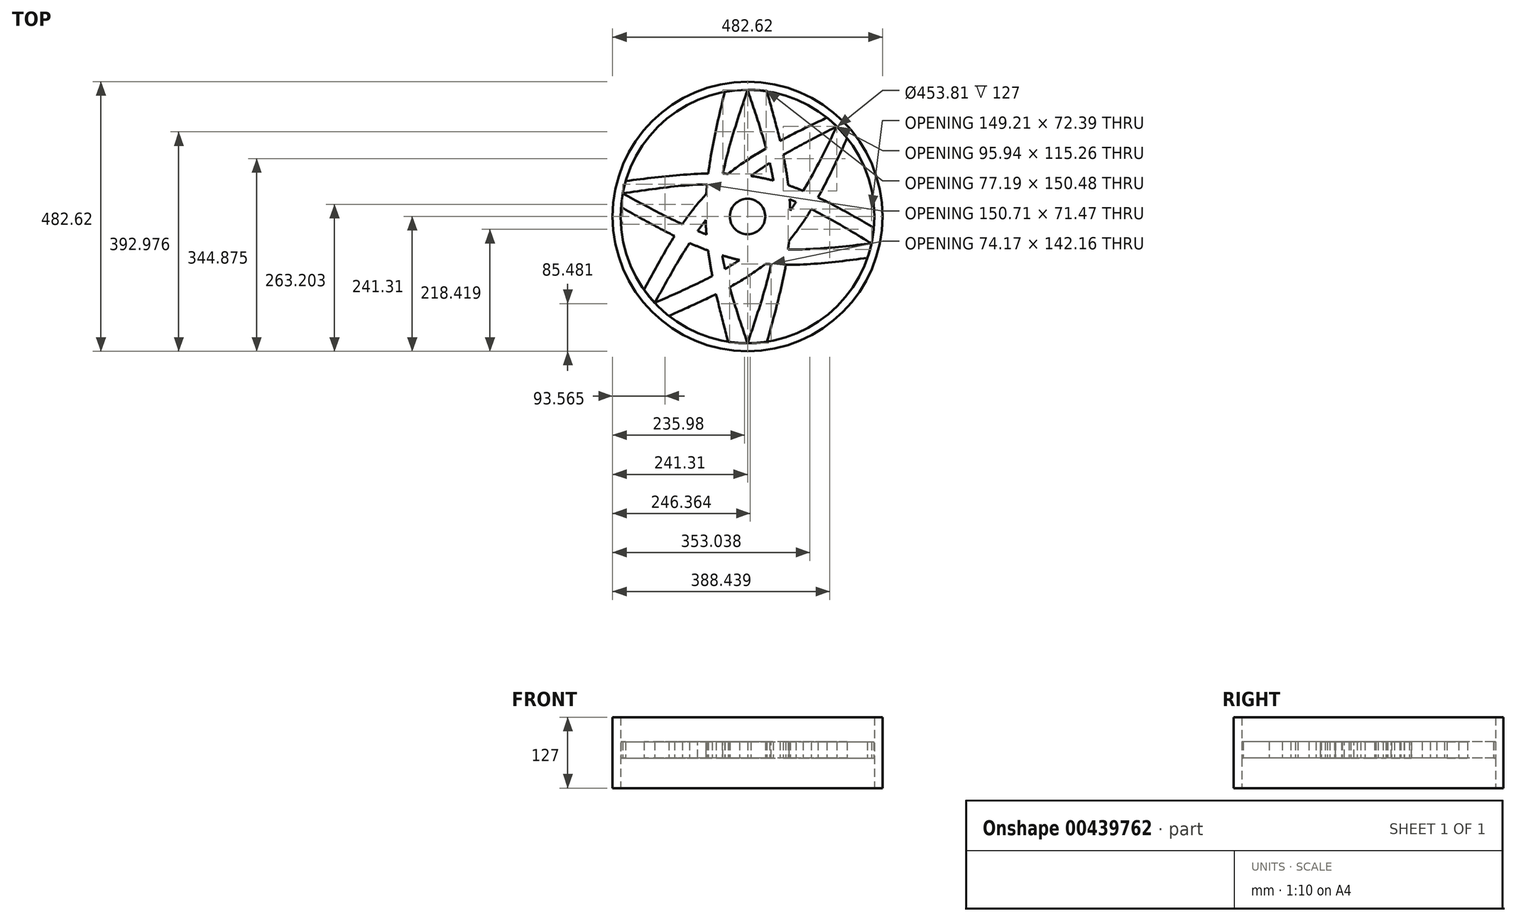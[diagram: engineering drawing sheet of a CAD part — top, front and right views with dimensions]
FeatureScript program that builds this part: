
annotation { "Feature Type Name" : "Feature", "Feature Type Description" : "" }
export const myFeature = defineFeature(function(context is Context, id is Id, definition is map)
    precondition{}
    {
        {
            var Q0;
            Q0=qCreatedBy(makeId("Top.planeOp"),FACE);
            var sketch = newSketch(context, id + "F0", { "sketchPlane" : qUnion([Q0])});
            skCircle(sketch, "E0", {"center": v(0, 0) * mm, "radius": 241.31 * mm});
            skCircle(sketch, "E1", {"center": v(0, 0) * mm, "radius": 31.77 * mm});
            skCircle(sketch, "E2", {"center": v(0, 0) * mm, "radius": 226.9 * mm});
            skFitSpline(sketch, "E3", {"points": [v(0, 226.9) * mm, v(-51.98, 0) * mm, v(0, -226.9) * mm], "startDerivative": vector(-152.5, -453.81) * mm, "endDerivative": vector(152.5, -453.81) * mm});
            skFitSpline(sketch, "E4", {"points": [v(0, 226.9) * mm, v(51.98, 0) * mm, v(0, -226.9) * mm], "startDerivative": vector(152.5, -453.81) * mm, "endDerivative": vector(-152.5, -453.81) * mm});
            skFitSpline(sketch, "E5", {"points": [v(-41.03, 223.17) * mm, v(-75, 0) * mm, v(-34.75, -224.23) * mm], "startDerivative": vector(-105.1, -447.44) * mm, "endDerivative": vector(117.58, -447.2) * mm});
            skFitSpline(sketch, "E6", {"points": [v(34.55, 224.26) * mm, v(76.47, 0) * mm, v(34.75, -224.23) * mm], "startDerivative": vector(125.73, -448.2) * mm, "endDerivative": vector(-125.27, -448.46) * mm});
            skFitSpline(sketch, "E7", {"points": [v(159.7, 161.2) * mm, v(-35.94, 37.55) * mm, v(-166, -154.7) * mm], "startDerivative": vector(-422.02, -215.9) * mm, "endDerivative": vector(-229.15, -415.66) * mm});
            skFitSpline(sketch, "E8", {"points": [v(142, 177) * mm, v(-58.52, 55.73) * mm, v(-185.22, -131.08) * mm], "startDerivative": vector(-432.84, -205.47) * mm, "endDerivative": vector(-220.65, -410.99) * mm});
            skFitSpline(sketch, "E9", {"points": [v(159.7, 161.2) * mm, v(32.57, -40.5) * mm, v(-166, -154.7) * mm], "startDerivative": vector(-208.67, -433.82) * mm, "endDerivative": vector(-442.51, -198.17) * mm});
            skFitSpline(sketch, "E10", {"points": [v(178.3, 140.33) * mm, v(54.6, -64.67) * mm, v(-140.7, -178.02) * mm], "startDerivative": vector(-205.55, -439.17) * mm, "endDerivative": vector(-432.46, -196.4) * mm});
            skFitSpline(sketch, "E11", {"points": [v(-223.1, 41.39) * mm, v(-6.94, -51.51) * mm, v(221.73, -48.18) * mm], "startDerivative": vector(421.7, -229.62) * mm, "endDerivative": vector(467.5, 51.27) * mm});
            skFitSpline(sketch, "E12", {"points": [v(-223.1, 41.39) * mm, v(10.2, 50.96) * mm, v(221.73, -48.18) * mm], "startDerivative": vector(476.9, 70.05) * mm, "endDerivative": vector(412.78, -249.16) * mm});
            skFitSpline(sketch, "E13", {"points": [v(-226.28, 16.81) * mm, v(-7.33, -79.24) * mm, v(214.47, -74.08) * mm], "startDerivative": vector(424, -239.26) * mm, "endDerivative": vector(457.26, 59.44) * mm});
            skFitSpline(sketch, "E14", {"points": [v(-217.83, 63.55) * mm, v(23.66, 69.54) * mm, v(226.02, -20.1) * mm], "startDerivative": vector(487.4, 61.66) * mm, "endDerivative": vector(399.3, -230.98) * mm});
            skSolve(sketch);
        }
        {
            var Q0;
            Q0=makeQuery(id+"F0.imprint","IMPRINT",FACE,{"disambiguationData":[TD([[makeQuery(id+"F0.imprint","IMPRINT",EDGE,{"derivedFrom":sQuery(id+"F0.wireOp",EDGE,"E0")}),1.0]])]});
            extrude(context, id + "F1", {"entities" : qUnion([Q0]), "depth" : 63.5 * mm, "hasSecondDirection" : true, "secondDirectionOppositeDirection" : true, "secondDirectionDepth" : 63.5 * mm});
        }
        {
            var Q0;
            {var subQ0=sQuery(id+"F0.wireOp",EDGE,"E11");var subQ5=sQuery(id+"F0.wireOp",EDGE,"E8");var subQ7=makeQuery(id+"F0.imprint","INTERSECT",VERTEX,{"derivedFrom":[subQ5,subQ0]});Q0=makeQuery(id+"F0.imprint","IMPRINT",FACE,{"disambiguationData":[TD([[makeQuery(id+"F0.imprint","IMPRINT",EDGE,{"disambiguationData":[TD([[subQ7,-1.0]])],"derivedFrom":subQ5}),-1.0]])]});}
            var Q1;
            {var subQ1=sQuery(id+"F0.wireOp",EDGE,"E2");var subQ3=sQuery(id+"F0.wireOp",EDGE,"E8");var subQ4=makeQuery(id+"F0.imprint","INTERSECT",VERTEX,{"disambiguationData":[OD(1.0)],"derivedFrom":[subQ1,subQ3]});Q1=makeQuery(id+"F0.imprint","IMPRINT",FACE,{"disambiguationData":[TD([[makeQuery(id+"F0.imprint","IMPRINT",EDGE,{"disambiguationData":[TD([[subQ4,1.0]])],"derivedFrom":subQ3}),1.0]])]});}
            var Q2;
            {var subQ0=sQuery(id+"F0.wireOp",EDGE,"E11");var subQ1=sQuery(id+"F0.wireOp",EDGE,"E7");var subQ2=makeQuery(id+"F0.imprint","INTERSECT",VERTEX,{"derivedFrom":[subQ1,subQ0]});Q2=makeQuery(id+"F0.imprint","IMPRINT",FACE,{"disambiguationData":[TD([[makeQuery(id+"F0.imprint","IMPRINT",EDGE,{"disambiguationData":[TD([[subQ2,-1.0]])],"derivedFrom":subQ1}),-1.0]])]});}
            var Q3;
            {var subQ0=sQuery(id+"F0.wireOp",EDGE,"E9");var subQ5=sQuery(id+"F0.wireOp",EDGE,"E5");var subQ6=makeQuery(id+"F0.imprint","INTERSECT",VERTEX,{"derivedFrom":[subQ5,subQ0]});Q3=makeQuery(id+"F0.imprint","IMPRINT",FACE,{"disambiguationData":[TD([[makeQuery(id+"F0.imprint","IMPRINT",EDGE,{"disambiguationData":[TD([[subQ6,-1.0]])],"derivedFrom":subQ5}),-1.0]])]});}
            var Q4;
            {var subQ0=sQuery(id+"F0.wireOp",EDGE,"E9");var subQ1=sQuery(id+"F0.wireOp",EDGE,"E3");var subQ2=makeQuery(id+"F0.imprint","INTERSECT",VERTEX,{"derivedFrom":[subQ1,subQ0]});Q4=makeQuery(id+"F0.imprint","IMPRINT",FACE,{"disambiguationData":[TD([[makeQuery(id+"F0.imprint","IMPRINT",EDGE,{"disambiguationData":[TD([[subQ2,-1.0]])],"derivedFrom":subQ1}),-1.0]])]});}
            var Q5;
            {var subQ1=sQuery(id+"F0.wireOp",EDGE,"E2");var subQ3=sQuery(id+"F0.wireOp",EDGE,"E5");var subQ4=makeQuery(id+"F0.imprint","INTERSECT",VERTEX,{"disambiguationData":[OD(1.0)],"derivedFrom":[subQ1,subQ3]});Q5=makeQuery(id+"F0.imprint","IMPRINT",FACE,{"disambiguationData":[TD([[makeQuery(id+"F0.imprint","IMPRINT",EDGE,{"disambiguationData":[TD([[subQ4,1.0]])],"derivedFrom":subQ3}),1.0]])]});}
            var Q6;
            {var subQ0=sQuery(id+"F0.wireOp",EDGE,"E11");var subQ1=sQuery(id+"F0.wireOp",EDGE,"E4");var subQ2=makeQuery(id+"F0.imprint","INTERSECT",VERTEX,{"derivedFrom":[subQ1,subQ0]});Q6=makeQuery(id+"F0.imprint","IMPRINT",FACE,{"disambiguationData":[TD([[makeQuery(id+"F0.imprint","IMPRINT",EDGE,{"disambiguationData":[TD([[subQ2,-1.0]])],"derivedFrom":subQ1}),1.0]])]});}
            var Q7;
            {var subQ3=sQuery(id+"F0.wireOp",EDGE,"E14");var subQ5=sQuery(id+"F0.wireOp",EDGE,"E10");var subQ7=makeQuery(id+"F0.imprint","INTERSECT",VERTEX,{"derivedFrom":[subQ5,subQ3]});Q7=makeQuery(id+"F0.imprint","IMPRINT",FACE,{"disambiguationData":[TD([[makeQuery(id+"F0.imprint","IMPRINT",EDGE,{"disambiguationData":[TD([[subQ7,-1.0]])],"derivedFrom":subQ5}),1.0]])]});}
            var Q8;
            {var subQ1=sQuery(id+"F0.wireOp",EDGE,"E2");var subQ3=sQuery(id+"F0.wireOp",EDGE,"E10");var subQ4=makeQuery(id+"F0.imprint","INTERSECT",VERTEX,{"disambiguationData":[OD(0.0)],"derivedFrom":[subQ1,subQ3]});Q8=makeQuery(id+"F0.imprint","IMPRINT",FACE,{"disambiguationData":[TD([[makeQuery(id+"F0.imprint","IMPRINT",EDGE,{"disambiguationData":[TD([[subQ4,-1.0]])],"derivedFrom":subQ3}),-1.0]])]});}
            var Q9;
            {var subQ0=sQuery(id+"F0.wireOp",EDGE,"E14");var subQ1=sQuery(id+"F0.wireOp",EDGE,"E9");var subQ2=makeQuery(id+"F0.imprint","INTERSECT",VERTEX,{"derivedFrom":[subQ1,subQ0]});Q9=makeQuery(id+"F0.imprint","IMPRINT",FACE,{"disambiguationData":[TD([[makeQuery(id+"F0.imprint","IMPRINT",EDGE,{"disambiguationData":[TD([[subQ2,-1.0]])],"derivedFrom":subQ1}),1.0]])]});}
            var Q10;
            {var subQ3=sQuery(id+"F0.wireOp",EDGE,"E10");var subQ7=sQuery(id+"F0.wireOp",EDGE,"E4");var subQ8=makeQuery(id+"F0.imprint","INTERSECT",VERTEX,{"derivedFrom":[subQ7,subQ3]});Q10=makeQuery(id+"F0.imprint","IMPRINT",FACE,{"disambiguationData":[TD([[makeQuery(id+"F0.imprint","IMPRINT",EDGE,{"disambiguationData":[TD([[subQ8,-1.0]])],"derivedFrom":subQ7}),1.0]])]});}
            var Q11;
            {var subQ1=sQuery(id+"F0.wireOp",EDGE,"E2");var subQ3=sQuery(id+"F0.wireOp",EDGE,"E6");var subQ4=makeQuery(id+"F0.imprint","INTERSECT",VERTEX,{"disambiguationData":[OD(1.0)],"derivedFrom":[subQ1,subQ3]});Q11=makeQuery(id+"F0.imprint","IMPRINT",FACE,{"disambiguationData":[TD([[makeQuery(id+"F0.imprint","IMPRINT",EDGE,{"disambiguationData":[TD([[subQ4,1.0]])],"derivedFrom":subQ3}),-1.0]])]});}
            var Q12;
            {var subQ0=sQuery(id+"F0.wireOp",EDGE,"E11");var subQ5=sQuery(id+"F0.wireOp",EDGE,"E6");var subQ7=makeQuery(id+"F0.imprint","INTERSECT",VERTEX,{"derivedFrom":[subQ5,subQ0]});Q12=makeQuery(id+"F0.imprint","IMPRINT",FACE,{"disambiguationData":[TD([[makeQuery(id+"F0.imprint","IMPRINT",EDGE,{"disambiguationData":[TD([[subQ7,-1.0]])],"derivedFrom":subQ5}),1.0]])]});}
            var Q13;
            {var subQ3=sQuery(id+"F0.wireOp",EDGE,"E8");var subQ5=sQuery(id+"F0.wireOp",EDGE,"E6");var subQ7=makeQuery(id+"F0.imprint","INTERSECT",VERTEX,{"derivedFrom":[subQ5,subQ3]});Q13=makeQuery(id+"F0.imprint","IMPRINT",FACE,{"disambiguationData":[TD([[makeQuery(id+"F0.imprint","IMPRINT",EDGE,{"disambiguationData":[TD([[subQ7,-1.0]])],"derivedFrom":subQ5}),1.0]])]});}
            var Q14;
            {var subQ0=sQuery(id+"F0.wireOp",EDGE,"E8");var subQ1=sQuery(id+"F0.wireOp",EDGE,"E4");var subQ2=makeQuery(id+"F0.imprint","INTERSECT",VERTEX,{"derivedFrom":[subQ1,subQ0]});Q14=makeQuery(id+"F0.imprint","IMPRINT",FACE,{"disambiguationData":[TD([[makeQuery(id+"F0.imprint","IMPRINT",EDGE,{"disambiguationData":[TD([[subQ2,-1.0]])],"derivedFrom":subQ1}),1.0]])]});}
            var Q15;
            {var subQ1=sQuery(id+"F0.wireOp",EDGE,"E2");var subQ3=sQuery(id+"F0.wireOp",EDGE,"E6");var subQ4=makeQuery(id+"F0.imprint","INTERSECT",VERTEX,{"disambiguationData":[OD(0.0)],"derivedFrom":[subQ1,subQ3]});Q15=makeQuery(id+"F0.imprint","IMPRINT",FACE,{"disambiguationData":[TD([[makeQuery(id+"F0.imprint","IMPRINT",EDGE,{"disambiguationData":[TD([[subQ4,-1.0]])],"derivedFrom":subQ3}),-1.0]])]});}
            var Q16;
            {var subQ1=sQuery(id+"F0.wireOp",EDGE,"E2");var subQ3=sQuery(id+"F0.wireOp",EDGE,"E5");var subQ4=makeQuery(id+"F0.imprint","INTERSECT",VERTEX,{"disambiguationData":[OD(0.0)],"derivedFrom":[subQ1,subQ3]});Q16=makeQuery(id+"F0.imprint","IMPRINT",FACE,{"disambiguationData":[TD([[makeQuery(id+"F0.imprint","IMPRINT",EDGE,{"disambiguationData":[TD([[subQ4,-1.0]])],"derivedFrom":subQ3}),1.0]])]});}
            var Q17;
            {var subQ5=sQuery(id+"F0.wireOp",EDGE,"E3");var subQ7=sQuery(id+"F0.wireOp",EDGE,"E14");var subQ9=makeQuery(id+"F0.imprint","INTERSECT",VERTEX,{"derivedFrom":[subQ5,subQ7]});Q17=makeQuery(id+"F0.imprint","IMPRINT",FACE,{"disambiguationData":[TD([[makeQuery(id+"F0.imprint","IMPRINT",EDGE,{"disambiguationData":[TD([[subQ9,-1.0]])],"derivedFrom":subQ5}),-1.0]])]});}
            var Q18;
            {var subQ3=sQuery(id+"F0.wireOp",EDGE,"E14");var subQ5=sQuery(id+"F0.wireOp",EDGE,"E5");var subQ6=makeQuery(id+"F0.imprint","INTERSECT",VERTEX,{"derivedFrom":[subQ5,subQ3]});Q18=makeQuery(id+"F0.imprint","IMPRINT",FACE,{"disambiguationData":[TD([[makeQuery(id+"F0.imprint","IMPRINT",EDGE,{"disambiguationData":[TD([[subQ6,-1.0]])],"derivedFrom":subQ5}),-1.0]])]});}
            var Q19;
            {var subQ0=sQuery(id+"F0.wireOp",EDGE,"E8");var subQ1=sQuery(id+"F0.wireOp",EDGE,"E3");var subQ2=makeQuery(id+"F0.imprint","INTERSECT",VERTEX,{"derivedFrom":[subQ1,subQ0]});Q19=makeQuery(id+"F0.imprint","IMPRINT",FACE,{"disambiguationData":[TD([[makeQuery(id+"F0.imprint","IMPRINT",EDGE,{"disambiguationData":[TD([[subQ2,-1.0]])],"derivedFrom":subQ1}),-1.0]])]});}
            var Q20;
            {var subQ0=sQuery(id+"F0.wireOp",EDGE,"E8");var subQ1=sQuery(id+"F0.wireOp",EDGE,"E5");var subQ2=makeQuery(id+"F0.imprint","INTERSECT",VERTEX,{"derivedFrom":[subQ1,subQ0]});Q20=makeQuery(id+"F0.imprint","IMPRINT",FACE,{"disambiguationData":[TD([[makeQuery(id+"F0.imprint","IMPRINT",EDGE,{"disambiguationData":[TD([[subQ2,-1.0]])],"derivedFrom":subQ1}),-1.0]])]});}
            var Q21;
            {var subQ0=sQuery(id+"F0.wireOp",EDGE,"E8");var subQ1=sQuery(id+"F0.wireOp",EDGE,"E4");var subQ2=makeQuery(id+"F0.imprint","INTERSECT",VERTEX,{"derivedFrom":[subQ1,subQ0]});Q21=makeQuery(id+"F0.imprint","IMPRINT",FACE,{"disambiguationData":[TD([[makeQuery(id+"F0.imprint","IMPRINT",EDGE,{"disambiguationData":[TD([[subQ2,-1.0]])],"derivedFrom":subQ1}),-1.0]])]});}
            var Q22;
            {var subQ0=sQuery(id+"F0.wireOp",EDGE,"E9");var subQ1=sQuery(id+"F0.wireOp",EDGE,"E3");var subQ2=makeQuery(id+"F0.imprint","INTERSECT",VERTEX,{"derivedFrom":[subQ1,subQ0]});Q22=makeQuery(id+"F0.imprint","IMPRINT",FACE,{"disambiguationData":[TD([[makeQuery(id+"F0.imprint","IMPRINT",EDGE,{"disambiguationData":[TD([[subQ2,-1.0]])],"derivedFrom":subQ1}),1.0]])]});}
            var Q23;
            {var subQ0=sQuery(id+"F0.wireOp",EDGE,"E9");var subQ1=sQuery(id+"F0.wireOp",EDGE,"E6");var subQ2=makeQuery(id+"F0.imprint","INTERSECT",VERTEX,{"derivedFrom":[subQ1,subQ0]});Q23=makeQuery(id+"F0.imprint","IMPRINT",FACE,{"disambiguationData":[TD([[makeQuery(id+"F0.imprint","IMPRINT",EDGE,{"disambiguationData":[TD([[subQ2,-1.0]])],"derivedFrom":subQ1}),1.0]])]});}
            var Q24;
            {var subQ0=sQuery(id+"F0.wireOp",EDGE,"E7");var subQ1=sQuery(id+"F0.wireOp",EDGE,"E4");var subQ2=makeQuery(id+"F0.imprint","INTERSECT",VERTEX,{"derivedFrom":[subQ1,subQ0]});Q24=makeQuery(id+"F0.imprint","IMPRINT",FACE,{"disambiguationData":[TD([[makeQuery(id+"F0.imprint","IMPRINT",EDGE,{"disambiguationData":[TD([[subQ2,-1.0]])],"derivedFrom":subQ1}),1.0]])]});}
            var Q25;
            {var subQ0=sQuery(id+"F0.wireOp",EDGE,"E13");var subQ1=sQuery(id+"F0.wireOp",EDGE,"E3");var subQ2=makeQuery(id+"F0.imprint","INTERSECT",VERTEX,{"derivedFrom":[subQ1,subQ0]});Q25=makeQuery(id+"F0.imprint","IMPRINT",FACE,{"disambiguationData":[TD([[makeQuery(id+"F0.imprint","IMPRINT",EDGE,{"disambiguationData":[TD([[subQ2,-1.0]])],"derivedFrom":subQ1}),-1.0]])]});}
            var Q26;
            {var subQ0=sQuery(id+"F0.wireOp",EDGE,"E11");var subQ1=sQuery(id+"F0.wireOp",EDGE,"E5");var subQ2=makeQuery(id+"F0.imprint","INTERSECT",VERTEX,{"derivedFrom":[subQ1,subQ0]});Q26=makeQuery(id+"F0.imprint","IMPRINT",FACE,{"disambiguationData":[TD([[makeQuery(id+"F0.imprint","IMPRINT",EDGE,{"disambiguationData":[TD([[subQ2,-1.0]])],"derivedFrom":subQ1}),-1.0]])]});}
            var Q27;
            {var subQ0=sQuery(id+"F0.wireOp",EDGE,"E14");var subQ1=sQuery(id+"F0.wireOp",EDGE,"E6");var subQ2=makeQuery(id+"F0.imprint","INTERSECT",VERTEX,{"derivedFrom":[subQ1,subQ0]});Q27=makeQuery(id+"F0.imprint","IMPRINT",FACE,{"disambiguationData":[TD([[makeQuery(id+"F0.imprint","IMPRINT",EDGE,{"disambiguationData":[TD([[subQ2,-1.0]])],"derivedFrom":subQ1}),1.0]])]});}
            var Q28;
            {var subQ0=sQuery(id+"F0.wireOp",EDGE,"E12");var subQ1=sQuery(id+"F0.wireOp",EDGE,"E5");var subQ2=makeQuery(id+"F0.imprint","INTERSECT",VERTEX,{"derivedFrom":[subQ1,subQ0]});Q28=makeQuery(id+"F0.imprint","IMPRINT",FACE,{"disambiguationData":[TD([[makeQuery(id+"F0.imprint","IMPRINT",EDGE,{"disambiguationData":[TD([[subQ2,-1.0]])],"derivedFrom":subQ1}),1.0]])]});}
            var Q29;
            {var subQ0=sQuery(id+"F0.wireOp",EDGE,"E14");var subQ1=sQuery(id+"F0.wireOp",EDGE,"E3");var subQ2=makeQuery(id+"F0.imprint","INTERSECT",VERTEX,{"derivedFrom":[subQ1,subQ0]});Q29=makeQuery(id+"F0.imprint","IMPRINT",FACE,{"disambiguationData":[TD([[makeQuery(id+"F0.imprint","IMPRINT",EDGE,{"disambiguationData":[TD([[subQ2,-1.0]])],"derivedFrom":subQ1}),1.0]])]});}
            var Q30;
            {var subQ0=sQuery(id+"F0.wireOp",EDGE,"E10");var subQ1=sQuery(id+"F0.wireOp",EDGE,"E4");var subQ2=makeQuery(id+"F0.imprint","INTERSECT",VERTEX,{"derivedFrom":[subQ1,subQ0]});Q30=makeQuery(id+"F0.imprint","IMPRINT",FACE,{"disambiguationData":[TD([[makeQuery(id+"F0.imprint","IMPRINT",EDGE,{"disambiguationData":[TD([[subQ2,-1.0]])],"derivedFrom":subQ1}),-1.0]])]});}
            var Q31;
            {var subQ0=sQuery(id+"F0.wireOp",EDGE,"E10");var subQ1=sQuery(id+"F0.wireOp",EDGE,"E6");var subQ2=makeQuery(id+"F0.imprint","INTERSECT",VERTEX,{"derivedFrom":[subQ1,subQ0]});Q31=makeQuery(id+"F0.imprint","IMPRINT",FACE,{"disambiguationData":[TD([[makeQuery(id+"F0.imprint","IMPRINT",EDGE,{"disambiguationData":[TD([[subQ2,-1.0]])],"derivedFrom":subQ1}),-1.0]])]});}
            var Q32;
            {var subQ0=sQuery(id+"F0.wireOp",EDGE,"E7");var subQ1=sQuery(id+"F0.wireOp",EDGE,"1zvcAR7V-laDh-ktkW-U6ED-mYYCZ9MNF7Ux");var subQ5=makeQuery(id+"F0.imprint","INTERSECT",VERTEX,{"disambiguationData":[OD(0.0)],"derivedFrom":[subQ1,subQ0]});Q32=makeQuery(id+"F0.imprint","IMPRINT",FACE,{"disambiguationData":[TD([[makeQuery(id+"F0.imprint","IMPRINT",EDGE,{"disambiguationData":[TD([[subQ5,-1.0]])],"derivedFrom":subQ1}),-1.0]])]});}
            var Q33;
            {var subQ1=sQuery(id+"F0.wireOp",EDGE,"E4");var subQ7=makeQuery(id+"F0.imprint","INTERSECT",VERTEX,{"derivedFrom":[sQuery(id+"F0.wireOp",EDGE,"1zvcAR7V-laDh-ktkW-U6ED-mYYCZ9MNF7Ux"),subQ1]});Q33=makeQuery(id+"F0.imprint","IMPRINT",FACE,{"disambiguationData":[TD([[makeQuery(id+"F0.imprint","IMPRINT",EDGE,{"disambiguationData":[TD([[subQ7,1.0]])],"derivedFrom":subQ1}),1.0]])]});}
            var Q34;
            {var subQ0=sQuery(id+"F0.wireOp",EDGE,"E11");var subQ1=sQuery(id+"F0.wireOp",EDGE,"1zvcAR7V-laDh-ktkW-U6ED-mYYCZ9MNF7Ux");var subQ2=makeQuery(id+"F0.imprint","INTERSECT",VERTEX,{"disambiguationData":[OD(0.0)],"derivedFrom":[subQ1,subQ0]});Q34=makeQuery(id+"F0.imprint","IMPRINT",FACE,{"disambiguationData":[TD([[makeQuery(id+"F0.imprint","IMPRINT",EDGE,{"disambiguationData":[TD([[subQ2,-1.0]])],"derivedFrom":subQ1}),-1.0]])]});}
            var Q35;
            {var subQ0=sQuery(id+"F0.wireOp",EDGE,"E11");var subQ1=sQuery(id+"F0.wireOp",EDGE,"E3");var subQ2=makeQuery(id+"F0.imprint","INTERSECT",VERTEX,{"derivedFrom":[subQ1,subQ0]});Q35=makeQuery(id+"F0.imprint","IMPRINT",FACE,{"disambiguationData":[TD([[makeQuery(id+"F0.imprint","IMPRINT",EDGE,{"disambiguationData":[TD([[subQ2,-1.0]])],"derivedFrom":subQ1}),1.0]])]});}
            var Q36;
            {var subQ0=sQuery(id+"F0.wireOp",EDGE,"E9");var subQ1=sQuery(id+"F0.wireOp",EDGE,"E4");var subQ2=makeQuery(id+"F0.imprint","INTERSECT",VERTEX,{"derivedFrom":[subQ1,subQ0]});Q36=makeQuery(id+"F0.imprint","IMPRINT",FACE,{"disambiguationData":[TD([[makeQuery(id+"F0.imprint","IMPRINT",EDGE,{"disambiguationData":[TD([[subQ2,-1.0]])],"derivedFrom":subQ1}),-1.0]])]});}
            var Q37;
            {var subQ0=sQuery(id+"F0.wireOp",EDGE,"E12");var subQ1=sQuery(id+"F0.wireOp",EDGE,"E4");var subQ2=makeQuery(id+"F0.imprint","INTERSECT",VERTEX,{"derivedFrom":[subQ1,subQ0]});Q37=makeQuery(id+"F0.imprint","IMPRINT",FACE,{"disambiguationData":[TD([[makeQuery(id+"F0.imprint","IMPRINT",EDGE,{"disambiguationData":[TD([[subQ2,-1.0]])],"derivedFrom":subQ1}),1.0]])]});}
            extrude(context, id + "F2", {"entities" : qUnion([Q0, Q1, Q2, Q3, Q4, Q5, Q6, Q7, Q8, Q9, Q10, Q11, Q12, Q13, Q14, Q15, Q16, Q17, Q18, Q19, Q20, Q21, Q22, Q23, Q24, Q25, Q26, Q27, Q28, Q29, Q30, Q31, Q32, Q33, Q34, Q35, Q36, Q37]), "depth" : 9.7 * mm, "hasSecondDirection" : true, "secondDirectionOppositeDirection" : true, "secondDirectionDepth" : 9.7 * mm});
        }
        {
            var Q0;
            {var subQ3=sQuery(id+"F0.wireOp",EDGE,"E12");var subQ5=sQuery(id+"F0.wireOp",EDGE,"E3");var subQ6=makeQuery(id+"F0.imprint","INTERSECT",VERTEX,{"derivedFrom":[subQ5,subQ3]});Q0=makeQuery(id+"F0.imprint","IMPRINT",FACE,{"disambiguationData":[TD([[makeQuery(id+"F0.imprint","IMPRINT",EDGE,{"disambiguationData":[TD([[subQ6,-1.0]])],"derivedFrom":subQ5}),-1.0]])]});}
            extrude(context, id + "F3", {"entities" : qUnion([Q0]), "depth" : 9.7 * mm, "hasSecondDirection" : true, "secondDirectionOppositeDirection" : true, "secondDirectionDepth" : 9.7 * mm});
        }
        {
            var Q0;
            {var subQ0=sQuery(id+"F0.wireOp",EDGE,"E14");var subQ1=sQuery(id+"F0.wireOp",EDGE,"E4");var subQ2=makeQuery(id+"F0.imprint","INTERSECT",VERTEX,{"derivedFrom":[subQ1,subQ0]});Q0=makeQuery(id+"F0.imprint","IMPRINT",FACE,{"disambiguationData":[TD([[makeQuery(id+"F0.imprint","IMPRINT",EDGE,{"disambiguationData":[TD([[subQ2,-1.0]])],"derivedFrom":subQ1}),1.0]])]});}
            var Q1;
            {var subQ0=sQuery(id+"F0.wireOp",EDGE,"E12");var subQ1=sQuery(id+"F0.wireOp",EDGE,"E4");var subQ2=makeQuery(id+"F0.imprint","INTERSECT",VERTEX,{"derivedFrom":[subQ1,subQ0]});Q1=makeQuery(id+"F0.imprint","IMPRINT",FACE,{"disambiguationData":[TD([[makeQuery(id+"F0.imprint","IMPRINT",EDGE,{"disambiguationData":[TD([[subQ2,-1.0]])],"derivedFrom":subQ1}),1.0]])]});}
            var Q2;
            {var subQ5=sQuery(id+"F0.wireOp",EDGE,"E9");var subQ6=sQuery(id+"F0.wireOp",EDGE,"E4");var subQ7=makeQuery(id+"F0.imprint","INTERSECT",VERTEX,{"derivedFrom":[subQ6,subQ5]});Q2=makeQuery(id+"F0.imprint","IMPRINT",FACE,{"disambiguationData":[TD([[makeQuery(id+"F0.imprint","IMPRINT",EDGE,{"disambiguationData":[TD([[subQ7,-1.0]])],"derivedFrom":subQ6}),1.0]])]});}
            var Q3;
            {var subQ0=sQuery(id+"F0.wireOp",EDGE,"E10");var subQ1=sQuery(id+"F0.wireOp",EDGE,"E4");var subQ2=makeQuery(id+"F0.imprint","INTERSECT",VERTEX,{"derivedFrom":[subQ1,subQ0]});Q3=makeQuery(id+"F0.imprint","IMPRINT",FACE,{"disambiguationData":[TD([[makeQuery(id+"F0.imprint","IMPRINT",EDGE,{"disambiguationData":[TD([[subQ2,-1.0]])],"derivedFrom":subQ1}),1.0]])]});}
            var Q4;
            {var subQ0=sQuery(id+"F0.wireOp",EDGE,"E11");var subQ1=sQuery(id+"F0.wireOp",EDGE,"E4");var subQ2=makeQuery(id+"F0.imprint","INTERSECT",VERTEX,{"derivedFrom":[subQ1,subQ0]});Q4=makeQuery(id+"F0.imprint","IMPRINT",FACE,{"disambiguationData":[TD([[makeQuery(id+"F0.imprint","IMPRINT",EDGE,{"disambiguationData":[TD([[subQ2,-1.0]])],"derivedFrom":subQ1}),-1.0]])]});}
            var Q5;
            {var subQ0=sQuery(id+"F0.wireOp",EDGE,"E11");var subQ1=sQuery(id+"F0.wireOp",EDGE,"E4");var subQ2=makeQuery(id+"F0.imprint","INTERSECT",VERTEX,{"derivedFrom":[subQ1,subQ0]});Q5=makeQuery(id+"F0.imprint","IMPRINT",FACE,{"disambiguationData":[TD([[makeQuery(id+"F0.imprint","IMPRINT",EDGE,{"disambiguationData":[TD([[subQ2,-1.0]])],"derivedFrom":subQ1}),1.0]])]});}
            var Q6;
            {var subQ0=sQuery(id+"F0.wireOp",EDGE,"E11");var subQ1=sQuery(id+"F0.wireOp",EDGE,"E3");var subQ2=makeQuery(id+"F0.imprint","INTERSECT",VERTEX,{"derivedFrom":[subQ1,subQ0]});Q6=makeQuery(id+"F0.imprint","IMPRINT",FACE,{"disambiguationData":[TD([[makeQuery(id+"F0.imprint","IMPRINT",EDGE,{"disambiguationData":[TD([[subQ2,-1.0]])],"derivedFrom":subQ1}),1.0]])]});}
            var Q7;
            {var subQ0=sQuery(id+"F0.wireOp",EDGE,"E11");var subQ1=sQuery(id+"F0.wireOp",EDGE,"E3");var subQ2=makeQuery(id+"F0.imprint","INTERSECT",VERTEX,{"derivedFrom":[subQ1,subQ0]});Q7=makeQuery(id+"F0.imprint","IMPRINT",FACE,{"disambiguationData":[TD([[makeQuery(id+"F0.imprint","IMPRINT",EDGE,{"disambiguationData":[TD([[subQ2,-1.0]])],"derivedFrom":subQ1}),-1.0]])]});}
            var Q8;
            {var subQ0=sQuery(id+"F0.wireOp",EDGE,"E7");var subQ1=sQuery(id+"F0.wireOp",EDGE,"E3");var subQ2=makeQuery(id+"F0.imprint","INTERSECT",VERTEX,{"derivedFrom":[subQ1,subQ0]});Q8=makeQuery(id+"F0.imprint","IMPRINT",FACE,{"disambiguationData":[TD([[makeQuery(id+"F0.imprint","IMPRINT",EDGE,{"disambiguationData":[TD([[subQ2,-1.0]])],"derivedFrom":subQ1}),-1.0]])]});}
            var Q9;
            {var subQ3=sQuery(id+"F0.wireOp",EDGE,"E12");var subQ5=sQuery(id+"F0.wireOp",EDGE,"E3");var subQ6=makeQuery(id+"F0.imprint","INTERSECT",VERTEX,{"derivedFrom":[subQ5,subQ3]});Q9=makeQuery(id+"F0.imprint","IMPRINT",FACE,{"disambiguationData":[TD([[makeQuery(id+"F0.imprint","IMPRINT",EDGE,{"disambiguationData":[TD([[subQ6,-1.0]])],"derivedFrom":subQ5}),-1.0]])]});}
            var Q10;
            {var subQ0=sQuery(id+"F0.wireOp",EDGE,"E12");var subQ1=sQuery(id+"F0.wireOp",EDGE,"E3");var subQ2=makeQuery(id+"F0.imprint","INTERSECT",VERTEX,{"derivedFrom":[subQ1,subQ0]});Q10=makeQuery(id+"F0.imprint","IMPRINT",FACE,{"disambiguationData":[TD([[makeQuery(id+"F0.imprint","IMPRINT",EDGE,{"disambiguationData":[TD([[subQ2,-1.0]])],"derivedFrom":subQ1}),1.0]])]});}
            var Q11;
            {var subQ0=sQuery(id+"F0.wireOp",EDGE,"E8");var subQ1=sQuery(id+"F0.wireOp",EDGE,"E3");var subQ2=makeQuery(id+"F0.imprint","INTERSECT",VERTEX,{"derivedFrom":[subQ1,subQ0]});Q11=makeQuery(id+"F0.imprint","IMPRINT",FACE,{"disambiguationData":[TD([[makeQuery(id+"F0.imprint","IMPRINT",EDGE,{"disambiguationData":[TD([[subQ2,-1.0]])],"derivedFrom":subQ1}),1.0]])]});}
            var Q12;
            {var subQ0=sQuery(id+"F0.wireOp",EDGE,"E14");var subQ1=sQuery(id+"F0.wireOp",EDGE,"E4");var subQ2=makeQuery(id+"F0.imprint","INTERSECT",VERTEX,{"derivedFrom":[subQ1,subQ0]});Q12=makeQuery(id+"F0.imprint","IMPRINT",FACE,{"disambiguationData":[TD([[makeQuery(id+"F0.imprint","IMPRINT",EDGE,{"disambiguationData":[TD([[subQ2,-1.0]])],"derivedFrom":subQ1}),-1.0]])]});}
            var Q13;
            {var subQ0=sQuery(id+"F0.wireOp",EDGE,"E14");var subQ1=sQuery(id+"F0.wireOp",EDGE,"E6");var subQ2=makeQuery(id+"F0.imprint","INTERSECT",VERTEX,{"derivedFrom":[subQ1,subQ0]});Q13=makeQuery(id+"F0.imprint","IMPRINT",FACE,{"disambiguationData":[TD([[makeQuery(id+"F0.imprint","IMPRINT",EDGE,{"disambiguationData":[TD([[subQ2,-1.0]])],"derivedFrom":subQ1}),1.0]])]});}
            var Q14;
            {var subQ0=sQuery(id+"F0.wireOp",EDGE,"E8");var subQ1=sQuery(id+"F0.wireOp",EDGE,"E3");var subQ2=makeQuery(id+"F0.imprint","INTERSECT",VERTEX,{"derivedFrom":[subQ1,subQ0]});Q14=makeQuery(id+"F0.imprint","IMPRINT",FACE,{"disambiguationData":[TD([[makeQuery(id+"F0.imprint","IMPRINT",EDGE,{"disambiguationData":[TD([[subQ2,-1.0]])],"derivedFrom":subQ1}),-1.0]])]});}
            var Q15;
            {var subQ5=sQuery(id+"F0.wireOp",EDGE,"E3");var subQ7=sQuery(id+"F0.wireOp",EDGE,"E14");var subQ9=makeQuery(id+"F0.imprint","INTERSECT",VERTEX,{"derivedFrom":[subQ5,subQ7]});Q15=makeQuery(id+"F0.imprint","IMPRINT",FACE,{"disambiguationData":[TD([[makeQuery(id+"F0.imprint","IMPRINT",EDGE,{"disambiguationData":[TD([[subQ9,-1.0]])],"derivedFrom":subQ5}),-1.0]])]});}
            var Q16;
            {var subQ0=sQuery(id+"F0.wireOp",EDGE,"E12");var subQ1=sQuery(id+"F0.wireOp",EDGE,"E5");var subQ2=makeQuery(id+"F0.imprint","INTERSECT",VERTEX,{"derivedFrom":[subQ1,subQ0]});Q16=makeQuery(id+"F0.imprint","IMPRINT",FACE,{"disambiguationData":[TD([[makeQuery(id+"F0.imprint","IMPRINT",EDGE,{"disambiguationData":[TD([[subQ2,-1.0]])],"derivedFrom":subQ1}),1.0]])]});}
            var Q17;
            {var subQ0=sQuery(id+"F0.wireOp",EDGE,"E14");var subQ1=sQuery(id+"F0.wireOp",EDGE,"E3");var subQ2=makeQuery(id+"F0.imprint","INTERSECT",VERTEX,{"derivedFrom":[subQ1,subQ0]});Q17=makeQuery(id+"F0.imprint","IMPRINT",FACE,{"disambiguationData":[TD([[makeQuery(id+"F0.imprint","IMPRINT",EDGE,{"disambiguationData":[TD([[subQ2,-1.0]])],"derivedFrom":subQ1}),1.0]])]});}
            var Q18;
            {var subQ0=sQuery(id+"F0.wireOp",EDGE,"E10");var subQ1=sQuery(id+"F0.wireOp",EDGE,"E4");var subQ2=makeQuery(id+"F0.imprint","INTERSECT",VERTEX,{"derivedFrom":[subQ1,subQ0]});Q18=makeQuery(id+"F0.imprint","IMPRINT",FACE,{"disambiguationData":[TD([[makeQuery(id+"F0.imprint","IMPRINT",EDGE,{"disambiguationData":[TD([[subQ2,-1.0]])],"derivedFrom":subQ1}),-1.0]])]});}
            var Q19;
            {var subQ0=sQuery(id+"F0.wireOp",EDGE,"E10");var subQ1=sQuery(id+"F0.wireOp",EDGE,"E6");var subQ2=makeQuery(id+"F0.imprint","INTERSECT",VERTEX,{"derivedFrom":[subQ1,subQ0]});Q19=makeQuery(id+"F0.imprint","IMPRINT",FACE,{"disambiguationData":[TD([[makeQuery(id+"F0.imprint","IMPRINT",EDGE,{"disambiguationData":[TD([[subQ2,-1.0]])],"derivedFrom":subQ1}),-1.0]])]});}
            extrude(context, id + "F4", {"entities" : qUnion([Q0, Q1, Q2, Q3, Q4, Q5, Q6, Q7, Q8, Q9, Q10, Q11, Q12, Q13, Q14, Q15, Q16, Q17, Q18, Q19]), "depth" : 9.7 * mm, "hasSecondDirection" : true, "secondDirectionOppositeDirection" : true, "secondDirectionDepth" : 9.7 * mm});
        }
        {
            var Q0;
            Q0=makeQuery(id+"F0.imprint","IMPRINT",FACE,{"disambiguationData":[TD([[makeQuery(id+"F0.imprint","IMPRINT",EDGE,{"derivedFrom":sQuery(id+"F0.wireOp",EDGE,"E1")}),-1.0]])]});
            extrude(context, id + "F5", {"entities" : qUnion([Q0]), "depth" : 9.7 * mm, "hasSecondDirection" : true, "secondDirectionOppositeDirection" : true, "secondDirectionDepth" : 9.7 * mm});
        }
        {
            var Q0;
            Q0=makeQuery(id+"F2.opExtrude","CAP_FACE",FACE,{"disambiguationData":[OSD([sQuery(id+"F0.wireOp",EDGE,"E2"),sQuery(id+"F0.wireOp",EDGE,"E5"),sQuery(id+"F0.wireOp",EDGE,"E7"),sQuery(id+"F0.wireOp",EDGE,"E8"),sQuery(id+"F0.wireOp",EDGE,"E11"),sQuery(id+"F0.wireOp",EDGE,"E13")])],"isStart":false});
            extrude(context, id + "F6", {"entities" : qUnion([Q0]), "operationType" : NewBodyOperationType.ADD, "depth" : 9.7 * mm, "hasSecondDirection" : true, "secondDirectionOppositeDirection" : true, "secondDirectionDepth" : 9.7 * mm});
        }
        {
            var Q0;
            Q0=makeQuery(id+"F2.opExtrude","CAP_FACE",FACE,{"disambiguationData":[OSD([sQuery(id+"F0.wireOp",EDGE,"E2"),sQuery(id+"F0.wireOp",EDGE,"E4"),sQuery(id+"F0.wireOp",EDGE,"E6"),sQuery(id+"F0.wireOp",EDGE,"E7"),sQuery(id+"F0.wireOp",EDGE,"E8"),sQuery(id+"F0.wireOp",EDGE,"E14")])],"isStart":false});
            extrude(context, id + "F7", {"entities" : qUnion([Q0]), "operationType" : NewBodyOperationType.ADD, "depth" : 9.7 * mm, "hasSecondDirection" : true, "secondDirectionOppositeDirection" : true, "secondDirectionDepth" : 9.7 * mm});
        }
        {
            var Q0;
            {var subQ0=sQuery(id+"F0.wireOp",EDGE,"E14");var subQ1=sQuery(id+"F0.wireOp",EDGE,"E13");var subQ2=sQuery(id+"F0.wireOp",EDGE,"E12");var subQ3=sQuery(id+"F0.wireOp",EDGE,"E9");var subQ4=sQuery(id+"F0.wireOp",EDGE,"E7");var subQ5=sQuery(id+"F0.wireOp",EDGE,"E6");var subQ6=sQuery(id+"F0.wireOp",EDGE,"E5");var subQ7=sQuery(id+"F0.wireOp",EDGE,"E3");var subQ8=sQuery(id+"F0.wireOp",EDGE,"E8");var subQ9=sQuery(id+"F0.wireOp",EDGE,"E10");var subQ10=sQuery(id+"F0.wireOp",EDGE,"E2");Q0=makeQuery(id+"F7.boolean.opBoolean","MERGE",FACE,{"derivedFrom":[makeQuery(id+"F2.opExtrude","CAP_FACE",FACE,{"disambiguationData":[OSD([subQ10,subQ5,subQ3,subQ9,subQ2,subQ0])],"isStart":false}),makeQuery(id+"F6.boolean.opBoolean","MERGE",FACE,{"derivedFrom":[makeQuery(id+"F2.opExtrude","CAP_FACE",FACE,{"disambiguationData":[OSD([subQ10,subQ7,subQ6,subQ8,subQ2,subQ0])],"isStart":false}),makeQuery(id+"F2.opExtrude","CAP_FACE",FACE,{"disambiguationData":[OSD([subQ10,subQ7,subQ6,subQ3,subQ9,subQ1])],"isStart":false}),makeQuery(id+"F3.opExtrude","CAP_FACE",FACE,{"disambiguationData":[OSD([subQ7,subQ6,subQ4,subQ8,subQ2])],"isStart":false}),makeQuery(id+"F4.opExtrude","CAP_FACE",FACE,{"disambiguationData":[OSD([subQ7,sQuery(id+"F0.wireOp",EDGE,"E4"),subQ6,subQ5,subQ4,subQ3,sQuery(id+"F0.wireOp",EDGE,"E11"),subQ2,subQ1,subQ0])],"isStart":false})]})]});}
            extrude(context, id + "F8", {"entities" : qUnion([Q0]), "operationType" : NewBodyOperationType.ADD, "depth" : 9.7 * mm, "hasSecondDirection" : true, "secondDirectionOppositeDirection" : true, "secondDirectionDepth" : 9.7 * mm});
        }
        {
            var Q0;
            {var subQ0=sQuery(id+"F0.wireOp",EDGE,"E11");var subQ1=sQuery(id+"F0.wireOp",EDGE,"E9");var subQ2=sQuery(id+"F0.wireOp",EDGE,"E4");Q0=makeQuery(id+"F8.boolean.opBoolean","MERGE",FACE,{"derivedFrom":[makeQuery(id+"F2.opExtrude","CAP_FACE",FACE,{"disambiguationData":[OSD([subQ2,subQ1,subQ0])],"isStart":false}),makeQuery(id+"F5.opExtrude","CAP_FACE",FACE,{"disambiguationData":[OSD([sQuery(id+"F0.wireOp",EDGE,"E1"),sQuery(id+"F0.wireOp",EDGE,"E3"),subQ2,sQuery(id+"F0.wireOp",EDGE,"E7"),subQ1,subQ0,sQuery(id+"F0.wireOp",EDGE,"E12")])],"isStart":false})]});}
            extrude(context, id + "F9", {"entities" : qUnion([Q0]), "operationType" : NewBodyOperationType.ADD, "depth" : 9.7 * mm, "hasSecondDirection" : true, "secondDirectionOppositeDirection" : true, "secondDirectionDepth" : 9.7 * mm});
        }
        {
            var Q0;
            {var subQ0=sQuery(id+"F0.wireOp",EDGE,"E14");var subQ1=sQuery(id+"F0.wireOp",EDGE,"E13");var subQ2=sQuery(id+"F0.wireOp",EDGE,"E12");var subQ3=sQuery(id+"F0.wireOp",EDGE,"E11");var subQ4=sQuery(id+"F0.wireOp",EDGE,"E9");var subQ5=sQuery(id+"F0.wireOp",EDGE,"E7");var subQ6=sQuery(id+"F0.wireOp",EDGE,"E6");var subQ7=sQuery(id+"F0.wireOp",EDGE,"E5");var subQ8=sQuery(id+"F0.wireOp",EDGE,"E4");var subQ9=sQuery(id+"F0.wireOp",EDGE,"E3");var subQ10=sQuery(id+"F0.wireOp",EDGE,"E8");var subQ11=sQuery(id+"F0.wireOp",EDGE,"E10");var subQ12=sQuery(id+"F0.wireOp",EDGE,"E2");Q0=makeQuery(id+"F8.boolean.opBoolean","MERGE",FACE,{"disambiguationData":[OD(1.0)],"derivedFrom":[makeQuery(id+"F2.opExtrude","CAP_FACE",FACE,{"disambiguationData":[OSD([subQ12,subQ8,subQ6,subQ11,subQ3,subQ1])],"isStart":false}),makeQuery(id+"F7.boolean.opBoolean","MERGE",FACE,{"derivedFrom":[makeQuery(id+"F2.opExtrude","CAP_FACE",FACE,{"disambiguationData":[OSD([subQ12,subQ6,subQ4,subQ11,subQ2,subQ0])],"isStart":false}),makeQuery(id+"F6.boolean.opBoolean","MERGE",FACE,{"derivedFrom":[makeQuery(id+"F2.opExtrude","CAP_FACE",FACE,{"disambiguationData":[OSD([subQ12,subQ9,subQ7,subQ10,subQ2,subQ0])],"isStart":false}),makeQuery(id+"F2.opExtrude","CAP_FACE",FACE,{"disambiguationData":[OSD([subQ12,subQ9,subQ7,subQ4,subQ11,subQ1])],"isStart":false}),makeQuery(id+"F3.opExtrude","CAP_FACE",FACE,{"disambiguationData":[OSD([subQ9,subQ7,subQ5,subQ10,subQ2])],"isStart":false}),makeQuery(id+"F4.opExtrude","CAP_FACE",FACE,{"disambiguationData":[OSD([subQ9,subQ8,subQ7,subQ6,subQ5,subQ4,subQ3,subQ2,subQ1,subQ0])],"isStart":false})]})]})]});}
            extrude(context, id + "F10", {"entities" : qUnion([Q0]), "operationType" : NewBodyOperationType.ADD, "depth" : 9.7 * mm, "hasSecondDirection" : true, "secondDirectionOppositeDirection" : true, "secondDirectionDepth" : 9.7 * mm});
        }
        {
            var Q0;
            {var subQ0=sQuery(id+"F0.wireOp",EDGE,"E14");var subQ1=sQuery(id+"F0.wireOp",EDGE,"E13");var subQ2=sQuery(id+"F0.wireOp",EDGE,"E12");var subQ3=sQuery(id+"F0.wireOp",EDGE,"E11");var subQ4=sQuery(id+"F0.wireOp",EDGE,"E9");var subQ5=sQuery(id+"F0.wireOp",EDGE,"E7");var subQ6=sQuery(id+"F0.wireOp",EDGE,"E6");var subQ7=sQuery(id+"F0.wireOp",EDGE,"E5");var subQ8=sQuery(id+"F0.wireOp",EDGE,"E4");var subQ9=sQuery(id+"F0.wireOp",EDGE,"E3");var subQ10=sQuery(id+"F0.wireOp",EDGE,"E8");var subQ11=sQuery(id+"F0.wireOp",EDGE,"E10");var subQ12=sQuery(id+"F0.wireOp",EDGE,"E2");Q0=makeQuery(id+"F8.boolean.opBoolean","MERGE",FACE,{"disambiguationData":[OD(0.0)],"derivedFrom":[makeQuery(id+"F2.opExtrude","CAP_FACE",FACE,{"disambiguationData":[OSD([subQ12,subQ8,subQ6,subQ11,subQ3,subQ1])],"isStart":false}),makeQuery(id+"F7.boolean.opBoolean","MERGE",FACE,{"derivedFrom":[makeQuery(id+"F2.opExtrude","CAP_FACE",FACE,{"disambiguationData":[OSD([subQ12,subQ6,subQ4,subQ11,subQ2,subQ0])],"isStart":false}),makeQuery(id+"F6.boolean.opBoolean","MERGE",FACE,{"derivedFrom":[makeQuery(id+"F2.opExtrude","CAP_FACE",FACE,{"disambiguationData":[OSD([subQ12,subQ9,subQ7,subQ10,subQ2,subQ0])],"isStart":false}),makeQuery(id+"F2.opExtrude","CAP_FACE",FACE,{"disambiguationData":[OSD([subQ12,subQ9,subQ7,subQ4,subQ11,subQ1])],"isStart":false}),makeQuery(id+"F3.opExtrude","CAP_FACE",FACE,{"disambiguationData":[OSD([subQ9,subQ7,subQ5,subQ10,subQ2])],"isStart":false}),makeQuery(id+"F4.opExtrude","CAP_FACE",FACE,{"disambiguationData":[OSD([subQ9,subQ8,subQ7,subQ6,subQ5,subQ4,subQ3,subQ2,subQ1,subQ0])],"isStart":false})]})]})]});}
            extrude(context, id + "F11", {"entities" : qUnion([Q0]), "operationType" : NewBodyOperationType.ADD, "depth" : 9.7 * mm, "hasSecondDirection" : true, "secondDirectionOppositeDirection" : true, "secondDirectionDepth" : 9.7 * mm});
        }
    });
